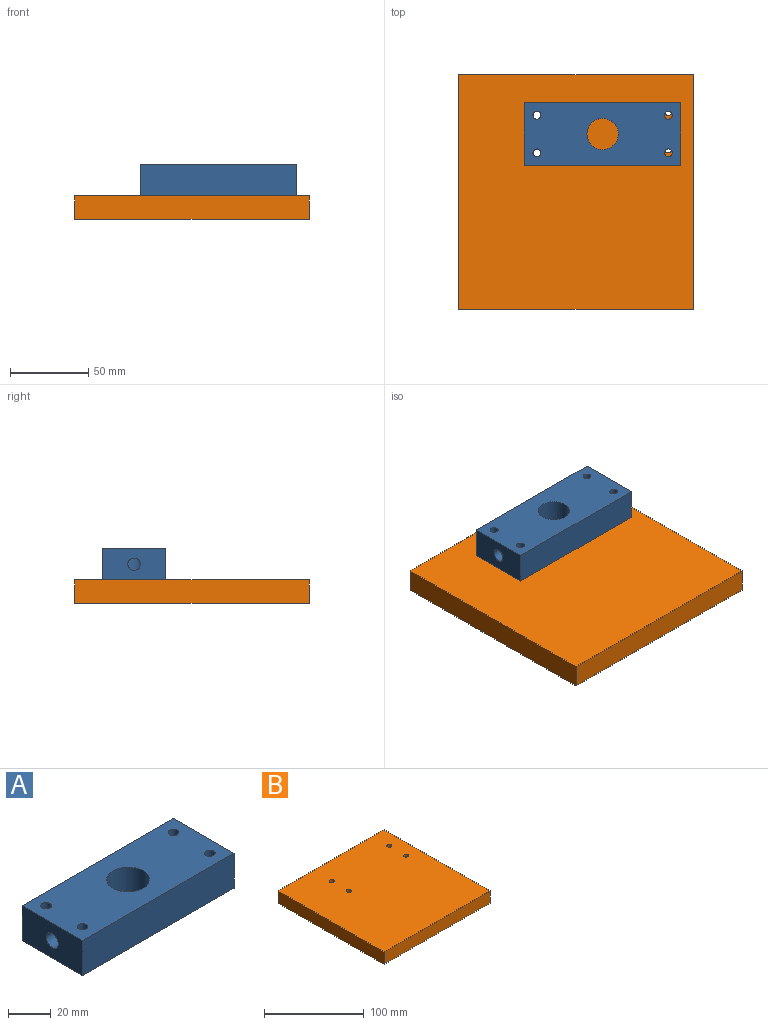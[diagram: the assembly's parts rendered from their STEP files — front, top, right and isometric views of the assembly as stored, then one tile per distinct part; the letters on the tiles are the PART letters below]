
ASSEMBLY  parts=2 mates=1
PART A: 12 faces, bbox 100x40x20 mm
  f0: plane 100x20mm, normal (0,1,0), area 2000mm2, adj f1,f8,f9,f10
  f1: plane 40x20mm, normal (-1,0,0), area 749.7mm2, adj f0,f2,f9,f10,f11
  f2: plane 100x20mm, normal (0,-1,0), area 2000mm2, adj f1,f8,f9,f10
  f3: cylinder r=10mm len=20mm, axis (0,0,-1), area 1205.2mm2, adj f9,f10,f11
  f4: cylinder r=2.5mm len=20mm, axis (0,0,-1), area 314.2mm2, adj f9,f10
  f5: cylinder r=2.5mm len=20mm, axis (0,0,-1), area 314.2mm2, adj f9,f10
  f6: cylinder r=2.5mm len=20mm, axis (0,0,-1), area 314.2mm2, adj f9,f10
  f7: cylinder r=2.5mm len=20mm, axis (0,0,-1), area 314.2mm2, adj f9,f10
  f8: plane 40x20mm, normal (1,0,0), area 800mm2, adj f0,f2,f9,f10
  f9: plane 100x40mm, normal (0,0,1), area 3607.3mm2, adj f0,f1,f2,f3,f4,f5,f6,f7
  f10: plane 100x40mm, normal (0,0,-1), area 3607.3mm2, adj f0,f1,f2,f3,f4,f5,f6,f7
  f11: cylinder r=4mm len=40.84mm, axis (-1,0,0), area 1015.7mm2, adj f1,f3
PART B: 10 faces, bbox 150x150x15 mm
  f0: plane 150x15mm, normal (0,1,0), area 2250mm2, adj f1,f7,f8,f9
  f1: plane 150x15mm, normal (-1,0,0), area 2250mm2, adj f0,f2,f8,f9
  f2: plane 150x15mm, normal (0,-1,0), area 2250mm2, adj f1,f7,f8,f9
  f3: cylinder r=2.5mm len=15mm, axis (0,0,-1), area 235.6mm2, adj f8,f9
  f4: cylinder r=2.5mm len=15mm, axis (0,0,-1), area 235.6mm2, adj f8,f9
  f5: cylinder r=2.5mm len=15mm, axis (0,0,-1), area 235.6mm2, adj f8,f9
  f6: cylinder r=2.5mm len=15mm, axis (0,0,-1), area 235.6mm2, adj f8,f9
  f7: plane 150x15mm, normal (1,0,0), area 2250mm2, adj f0,f2,f8,f9
  f8: plane 150x150mm, normal (0,0,1), area 22421.5mm2, adj f0,f1,f2,f3,f4,f5,f6,f7
  f9: plane 150x150mm, normal (0,0,-1), area 22421.5mm2, adj f0,f1,f2,f3,f4,f5,f6,f7
PLACE A t=(-2.55,90.96,15)mm
PLACE B at identity
MATE fastened A.f5 <-> B.f4  axis (0,0,-1) through (-49.2,109.77,15)mm
